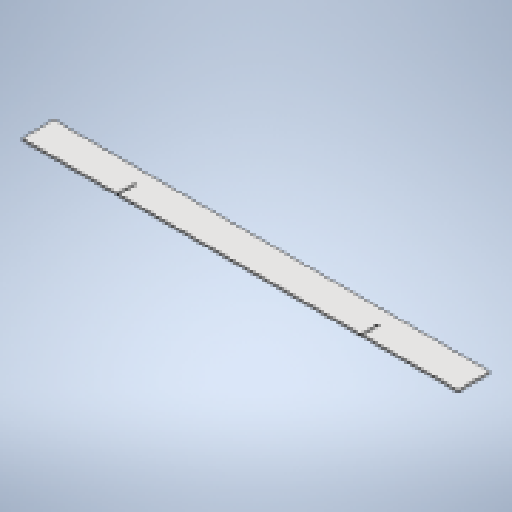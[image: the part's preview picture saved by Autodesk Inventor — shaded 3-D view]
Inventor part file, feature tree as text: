
AUTODESK INVENTOR PART (.ipt)
format: ipt  version: 2025 (Build 290162010, 162A)  size: 191,488 bytes
history: native  units: mm
features: sketch x3, extrude x2, sheet_metal_op x1, other x1, projected_geometry x1
ambient origin geometry x8: Origin, YZ Plane, XZ Plane, XY Plane, X Axis, Y Axis, Z Axis, Center Point
bodies: Body1 (feature_tree)
feature tree (8):
  sheet_metal_op  "Face1"
  extrude  "Extrusion1"  Depth=50.0mm
  extrude  "Extrusion2"  Depth=50.0mm
  sketch  "Sketch1"  dims[d16=50.0mm d17=800.0mm]
  other  "Plate2"
  sketch  "Sketch2"  dims[d18=50.0mm d19=50.0mm]
  sketch  "Sketch3"  dims[d20=3.0mm d21=190.0mm d22=3.0mm d23=26.0mm d24=10.0mm d25=0.0mm d26=190.0mm d27=26.0mm d28=3.0mm d29=75.0mm d30=75.0mm d31=0.0mm d32=0.0mm]
  projected_geometry  "Projected Loop1"
